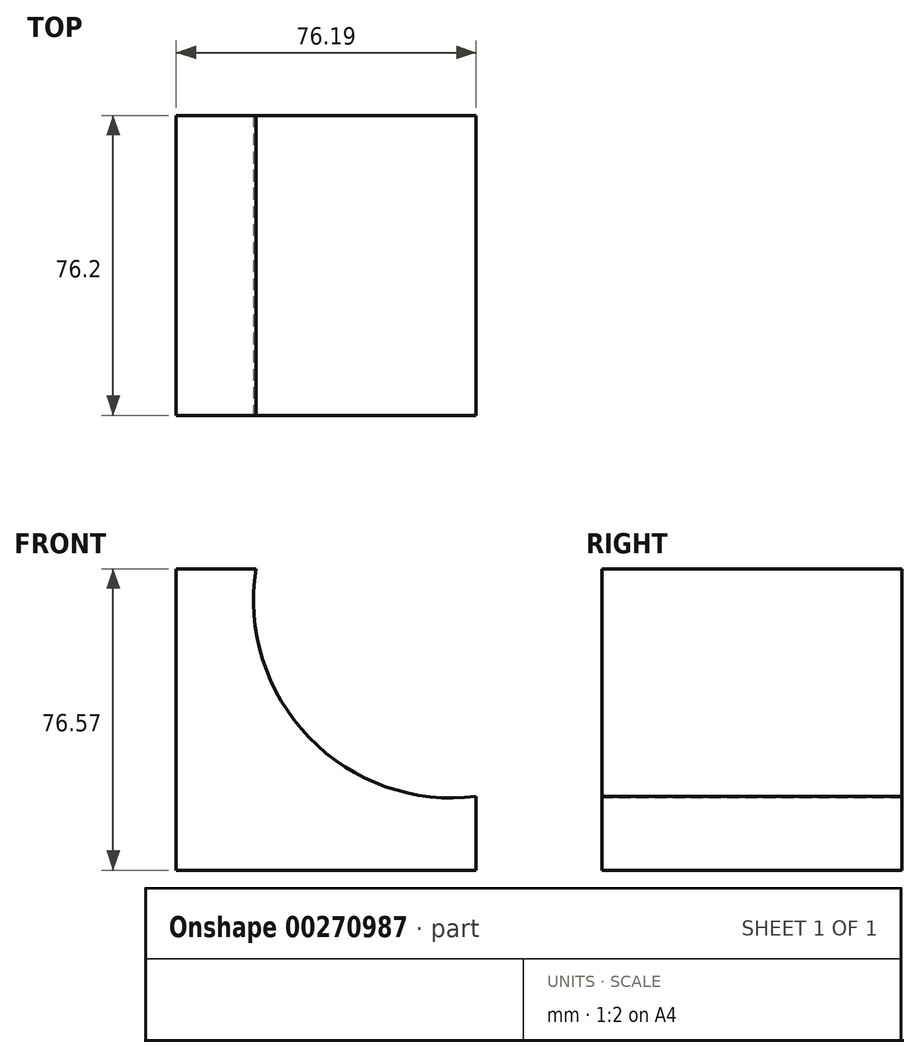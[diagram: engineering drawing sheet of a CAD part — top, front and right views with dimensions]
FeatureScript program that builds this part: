
annotation { "Feature Type Name" : "Feature", "Feature Type Description" : "" }
export const myFeature = defineFeature(function(context is Context, id is Id, definition is map)
    precondition{}
    {
        {
            var Q0;
            Q0=qCreatedBy(makeId("Front.planeOp"),FACE);
            var sketch = newSketch(context, id + "F0", { "sketchPlane" : qUnion([Q0])});
            skLineSegment(sketch, "E0.bottom", {"start": v(0, 0) * mm, "end": v(-76.2, 0) * mm});
            skLineSegment(sketch, "E0.top", {"start": v(0, 76.57) * mm, "end": v(-76.2, 76.57) * mm});
            skLineSegment(sketch, "E0.left", {"start": v(0, 0) * mm, "end": v(0, 76.57) * mm});
            skLineSegment(sketch, "E0.right", {"start": v(-76.2, 0) * mm, "end": v(-76.2, 76.57) * mm});
            skSolve(sketch);
        }
        {
            var Q0;
            Q0 = qSketchRegion(id + "F0", true);
            extrude(context, id + "F1", {"entities" : qUnion([Q0]), "depth" : 76.2 * mm});
        }
        {
            var Q0;
            Q0=makeQuery(id+"F1.opExtrude","CAP_FACE",FACE,{"disambiguationData":[OSD([sQuery(id+"F0.wireOp",EDGE,"E0.bottom"),sQuery(id+"F0.wireOp",EDGE,"E0.top"),sQuery(id+"F0.wireOp",EDGE,"E0.left"),sQuery(id+"F0.wireOp",EDGE,"E0.right")])],"isStart":false});
            var sketch = newSketch(context, id + "F2", { "sketchPlane" : qUnion([Q0])});
            skArc(sketch, "E1", {"start": v(-55.95, 76.57) * mm, "mid": v(-42.4, 33.69) * mm, "end": v(0, 18.71) * mm});
            skSolve(sketch);
        }
        {
            var Q0;
            Q0 = qSketchRegion(id + "F2", true);
            var Q1;
            {var subQ0=sQuery(id+"F2.wireOp",EDGE,"E1");Q1=makeQuery(id+"F2.imprint","IMPRINT",FACE,{"disambiguationData":[TD([[makeQuery(id+"F2.imprint","IMPRINT",EDGE,{"derivedFrom":subQ0}),1.0]])]});}
            extrude(context, id + "F3", {"entities" : qUnion([Q0, Q1]), "operationType" : NewBodyOperationType.REMOVE, "oppositeDirection" : true, "depth" : 76.2 * mm});
        }
    });
